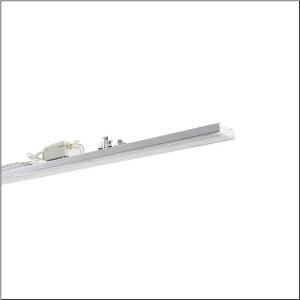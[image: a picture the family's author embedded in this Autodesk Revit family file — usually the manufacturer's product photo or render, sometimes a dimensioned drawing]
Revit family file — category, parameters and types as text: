
# Revit family: licross_11_recessed_extreme_mo_51te12dn49xge
name_source: partatom
category: Lighting Fixtures
units: mm (PartAtom-declared; Revit-internal decimal feet)

## family parameters
Cut with Voids When Loaded = No
Host = Face
Light Source = No
Part Type = Normal
Room Calculation Point = No
Round Connector Dimension = Use Diameter
Shared = No

## types (1)
- --- (1 x LED, 9140 lm, 50.1 W, 4000K)
    Apparent Load = 50 VA
    CIE Flux Codes = 67 92 99 100 100
    Color Rendering = 80
    Color Temperature = 4000K
    Default Elevation = 1800 mm
    Description = Licross 11 Recessed extreme MO, luminaire insert, of sheet steel, galvanised, coil coated, white, length: 1.500mm, width: 66mm, height: 67mm, LED rated luminous flux: 9.140lm, light colour: 840, SDCM (Standard Deviation of Colour Matching)MacAdam ≤ 2 SDCM (initial), control gear: DALI 2, with plug, 5-pole, with phase selection, mains connection: 220..240V, AC, 50/60Hz, rated input power: 50W, internal wiring halogen-free, primary optical cover: cover, of PMMA, light emission: direct distribution, primary light characteristic: symmetric, protection rating (complete): IP54, insulation class (complete): insulation class I (protective earthing), certification: CE, ENEC, VDE, UKCA, protection symbol: D if used in an environment with non-conductive dust loads with corresponding accessories, impact resistance: IK06, permissible ambient temperature for indoor applications: -25..+45°C, corresponds to IFS (International Featured Standards) requirements for safety and quality in the food industry, reducing of maximum allowable ambient temperature of 5°C with ceiling mounting, LABS conformity tested according to VDMA 24364:2018-05, The light source and the operating device comply with the requirements of the Ecodesign Regulation (EU) 2019/2020 and are replaceable in accordance with this regulation, packaging unit: 1 piece
    Height = 58 mm
    Lamp = 1 x LED
    Lamp Light Flux = 9140 lm
    Lamp Power = 50.1 W
    Lamp count = 1
    Length = 1500 mm
    Luminous efficacy = 182 lm/W
    Manufacturer = Siteco
    ModVariant = No
    Model = 51TE12DN49XGE
    Mounting Place = Ceiling
    Mounting Type = Pendant
    Number of Poles = 1
    OnlyDefault = Yes
    Power Factor = 1
    Product Name = Licross 11 Recessed extreme MO
    Product group = luminaire insert | ceiling pendant
    ProductGroupID = 901
    Protection Class = Protection class I
    Protection Degree = IP 54
    RLX_Detail_Level = 1
    RLX_Emergency_Light_Flux = 0 lm
    RLX_Emergency_Type = 0
    RLX_Emergency_Type_DB = No
    RlxData = <blob elided: 24781 chars, md5=05f105f4>
    Socket = socket
    Standby Power = 0 W
    System Light Flux = 9140 lm
    System Power = 50 W
    Type Comments = factory setting: luminous flux: 100 % | dim-lin: 254 | 334 mA
    Type Image = l_1296930.jpg
    URL = http://relux.com
    VarID = @adj_095835
    Voltage = 0 V
    Weight = 0.00 kg
    Width = 66 mm

## geometry (parser evidence)
native form markers: Blend x4, Sweep x10
no freeform markers — native parametric forms only
